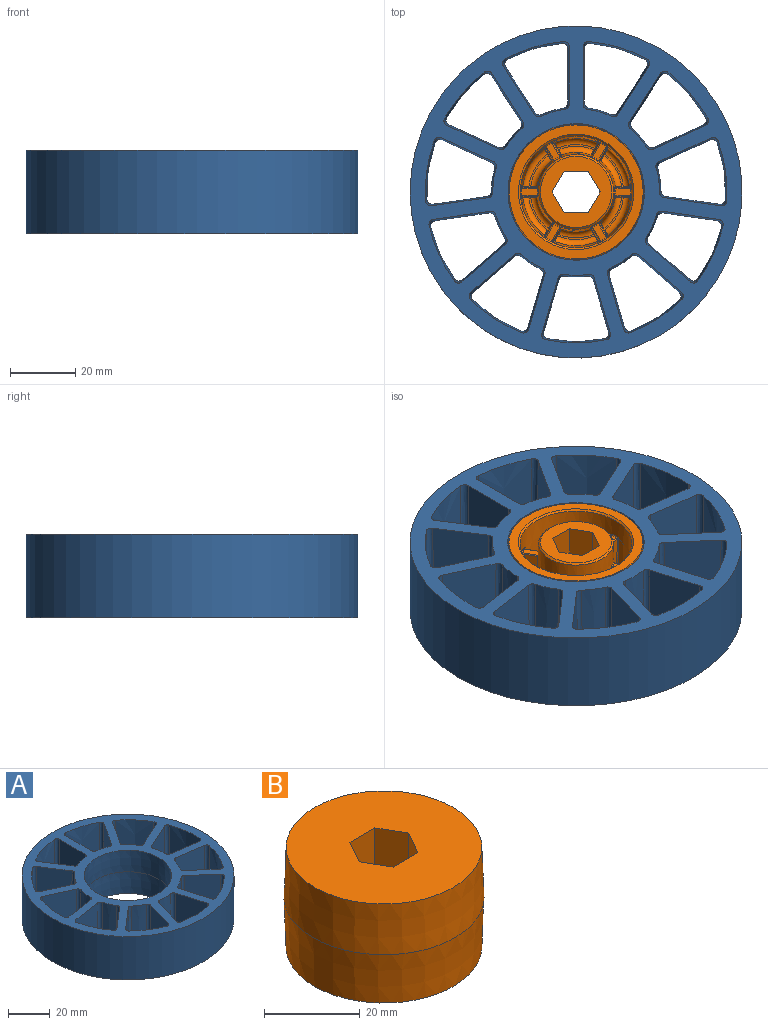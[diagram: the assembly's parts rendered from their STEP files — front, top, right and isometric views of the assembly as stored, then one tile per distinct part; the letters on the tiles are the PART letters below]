
ASSEMBLY  parts=2 mates=1
PART A: 93 faces, bbox 101.7x101.7x25.8 mm
  f0: cylinder r=50.8mm len=101.6mm, axis (0,0,-1), area 8107.3mm2, adj f25,f27
  f1: cone r=20.96mm half-angle=0.3deg, axis (0,0,1), area 1669.7mm2, adj f2,f27
  f2: cone r=20.89mm half-angle=0.3deg, axis (0,0,-1), area 1669.7mm2, adj f1,f25
  f3: cone r=45.72mm half-angle=1deg, axis (0,0,1), area 460.8mm2, adj f25,f27,f58,f59
  f4: cone r=25.97mm half-angle=1deg, axis (0,0,-1), area 186.1mm2, adj f25,f27,f80,f81
  f5: cone r=25.97mm half-angle=1deg, axis (0,0,-1), area 186.2mm2, adj f25,f27,f88,f89
  f6: cone r=45.72mm half-angle=1deg, axis (0,0,1), area 460.8mm2, adj f25,f27,f90,f91
  f7: cone r=45.72mm half-angle=1deg, axis (0,0,1), area 460.8mm2, adj f25,f27,f82,f83
  f8: cone r=25.97mm half-angle=1deg, axis (0,0,-1), area 186.2mm2, adj f25,f27,f76,f77
  f9: cone r=45.72mm half-angle=1deg, axis (0,0,1), area 460.8mm2, adj f25,f27,f78,f79
  f10: cone r=25.97mm half-angle=1deg, axis (0,0,-1), area 186.2mm2, adj f25,f27,f72,f73
  f11: cone r=45.72mm half-angle=1deg, axis (0,0,1), area 460.8mm2, adj f25,f27,f74,f75
  f12: cone r=25.97mm half-angle=1deg, axis (0,0,-1), area 186.2mm2, adj f25,f27,f68,f69
  f13: cone r=45.72mm half-angle=1deg, axis (0,0,1), area 460.8mm2, adj f25,f27,f70,f71
  f14: cone r=25.97mm half-angle=1deg, axis (0,0,-1), area 186.2mm2, adj f25,f27,f64,f65
  f15: cone r=45.72mm half-angle=1deg, axis (0,0,1), area 460.8mm2, adj f25,f27,f66,f67
  f16: cone r=25.97mm half-angle=1deg, axis (0,0,-1), area 186.2mm2, adj f25,f27,f60,f61
  f17: cone r=45.72mm half-angle=1deg, axis (0,0,1), area 460.8mm2, adj f25,f27,f62,f63
  f18: cone r=25.97mm half-angle=1deg, axis (0,0,-1), area 186.2mm2, adj f25,f27,f56,f57
  f19: cone r=25.97mm half-angle=1deg, axis (0,0,-1), area 186.2mm2, adj f25,f27,f52,f53
  f20: cone r=45.72mm half-angle=1deg, axis (0,0,1), area 460.8mm2, adj f25,f27,f54,f55
  f21: cone r=25.97mm half-angle=1deg, axis (0,0,-1), area 186.2mm2, adj f25,f27,f49,f50
  f22: cone r=45.72mm half-angle=1deg, axis (0,0,1), area 460.8mm2, adj f25,f27,f51,f92
  f23: plane 25.4x17.56mm, normal (1,0,0.02), area 435mm2, adj f25,f27,f85,f86
  f24: plane 25.4x17.56mm, normal (-1,0,0.02), area 435mm2, adj f25,f27,f50,f92
  f25: plane 101.66x101.66mm, normal (0,0,1), area 3063.9mm2, adj f0,f2,f3,f4,f5,f6,f7,f8
  f26: cone r=25.97mm half-angle=1deg, axis (0,0,-1), area 186.2mm2, adj f25,f27,f86,f87
  f27: plane 101.66x101.66mm, normal (0,0,-1), area 3415.8mm2, adj f0,f1,f3,f4,f5,f6,f7,f8
  f28: cone r=45.72mm half-angle=1deg, axis (0,0,1), area 460.8mm2, adj f25,f27,f84,f85
  f29: plane 25.4x14.77mm, normal (0.84,0.54,0.02), area 435mm2, adj f25,f27,f49,f51
  f30: plane 25.4x14.77mm, normal (-0.84,-0.54,0.02), area 435mm2, adj f25,f27,f53,f54
  f31: plane 25.4x15.97mm, normal (0.42,0.91,0.02), area 435mm2, adj f25,f27,f52,f55
  f32: plane 25.4x15.97mm, normal (-0.42,-0.91,0.02), area 435mm2, adj f25,f27,f57,f58
  f33: plane 25.4x17.38mm, normal (-0.14,0.99,0.02), area 435mm2, adj f25,f27,f56,f59
  f34: plane 25.4x17.38mm, normal (0.14,-0.99,0.02), area 435mm2, adj f25,f27,f61,f62
  f35: plane 25.4x13.27mm, normal (-0.65,0.76,0.02), area 435mm2, adj f25,f27,f60,f63
  f36: plane 25.4x13.27mm, normal (0.65,-0.76,0.02), area 435mm2, adj f25,f27,f65,f66
  f37: plane 25.4x16.85mm, normal (-0.96,0.28,0.02), area 435mm2, adj f25,f27,f64,f67
  f38: plane 25.4x16.85mm, normal (0.96,-0.28,0.02), area 435mm2, adj f25,f27,f69,f70
  f39: plane 25.4x16.85mm, normal (-0.96,-0.28,0.02), area 435mm2, adj f25,f27,f68,f71
  f40: plane 25.4x16.85mm, normal (0.96,0.28,0.02), area 435mm2, adj f25,f27,f73,f74
  f41: plane 25.4x13.27mm, normal (-0.65,-0.76,0.02), area 435mm2, adj f25,f27,f72,f75
  f42: plane 25.4x13.27mm, normal (0.65,0.76,0.02), area 435mm2, adj f25,f27,f77,f78
  f43: plane 25.4x17.38mm, normal (-0.14,-0.99,0.02), area 435mm2, adj f25,f27,f76,f79
  f44: plane 25.4x17.38mm, normal (0.14,0.99,0.02), area 435mm2, adj f25,f27,f81,f82
  f45: plane 25.4x15.97mm, normal (0.42,-0.91,0.02), area 435mm2, adj f25,f27,f80,f83
  f46: plane 25.4x15.97mm, normal (-0.42,0.91,0.02), area 435mm2, adj f25,f27,f89,f90
  f47: plane 25.4x14.77mm, normal (0.84,-0.54,0.02), area 435mm2, adj f25,f27,f88,f91
  f48: plane 25.4x14.77mm, normal (-0.84,0.54,0.02), area 435mm2, adj f25,f27,f84,f87
  f49: bspline ~25.41x2.15mm, area 57.6mm2, adj f21,f25,f27,f29
  f50: bspline ~25.41x1.96mm, area 57.6mm2, adj f21,f24,f25,f27
  f51: bspline ~25.41x2.43mm, area 66.9mm2, adj f22,f25,f27,f29
  f52: bspline ~25.41x2.17mm, area 57.6mm2, adj f19,f25,f27,f31
  f53: bspline ~25.41x2.15mm, area 57.6mm2, adj f19,f25,f27,f30
  f54: bspline ~25.75x2.43mm, area 66.9mm2, adj f20,f25,f27,f30
  f55: bspline ~25.75x2.44mm, area 66.9mm2, adj f20,f25,f27,f31
  f56: bspline ~25.73x1.95mm, area 57.6mm2, adj f18,f25,f27,f33
  f57: bspline ~25.73x2.13mm, area 57.6mm2, adj f18,f25,f27,f32
  f58: bspline ~25.75x2.41mm, area 66.9mm2, adj f3,f25,f27,f32
  f59: bspline ~25.41x2.23mm, area 66.9mm2, adj f3,f25,f27,f33
  f60: bspline ~25.73x2.13mm, area 57.6mm2, adj f16,f25,f27,f35
  f61: bspline ~25.41x2.07mm, area 57.6mm2, adj f16,f25,f27,f34
  f62: bspline ~25.41x2.31mm, area 66.9mm2, adj f17,f25,f27,f34
  f63: bspline ~25.75x2.4mm, area 66.9mm2, adj f17,f25,f27,f35
  f64: bspline ~25.73x2.14mm, area 57.6mm2, adj f14,f25,f27,f37
  f65: bspline ~25.73x2.09mm, area 57.6mm2, adj f14,f25,f27,f36
  f66: bspline ~25.41x2.36mm, area 66.9mm2, adj f15,f25,f27,f36
  f67: bspline ~25.75x2.4mm, area 66.9mm2, adj f15,f25,f27,f37
  f68: bspline ~25.41x2.05mm, area 57.6mm2, adj f12,f25,f27,f39
  f69: bspline ~25.41x2.05mm, area 57.6mm2, adj f12,f25,f27,f38
  f70: bspline ~25.41x2.34mm, area 66.9mm2, adj f13,f25,f27,f38
  f71: bspline ~25.41x2.34mm, area 66.9mm2, adj f13,f25,f27,f39
  f72: bspline ~25.73x2.09mm, area 57.6mm2, adj f10,f25,f27,f41
  f73: bspline ~25.73x2.14mm, area 57.6mm2, adj f10,f25,f27,f40
  f74: bspline ~25.75x2.4mm, area 66.9mm2, adj f11,f25,f27,f40
  f75: bspline ~25.41x2.36mm, area 66.9mm2, adj f11,f25,f27,f41
  f76: bspline ~25.41x2.07mm, area 57.6mm2, adj f8,f25,f27,f43
  f77: bspline ~25.73x2.13mm, area 57.6mm2, adj f8,f25,f27,f42
  f78: bspline ~25.75x2.4mm, area 66.9mm2, adj f9,f25,f27,f42
  f79: bspline ~25.41x2.31mm, area 66.9mm2, adj f9,f25,f27,f43
  f80: bspline ~25.73x2.13mm, area 57.6mm2, adj f4,f25,f27,f45
  f81: bspline ~25.41x1.94mm, area 57.6mm2, adj f4,f25,f27,f44
  f82: bspline ~25.41x2.23mm, area 66.9mm2, adj f7,f25,f27,f44
  f83: bspline ~25.75x2.41mm, area 66.9mm2, adj f7,f25,f27,f45
  f84: bspline ~25.41x2.43mm, area 66.9mm2, adj f25,f27,f28,f48
  f85: bspline ~25.41x2.18mm, area 66.9mm2, adj f23,f25,f27,f28
  f86: bspline ~25.41x1.96mm, area 57.6mm2, adj f23,f25,f26,f27
  f87: bspline ~25.41x2.15mm, area 57.6mm2, adj f25,f26,f27,f48
  f88: bspline ~25.41x2.15mm, area 57.6mm2, adj f5,f25,f27,f47
  f89: bspline ~25.41x2.17mm, area 57.6mm2, adj f5,f25,f27,f46
  f90: bspline ~25.75x2.44mm, area 66.9mm2, adj f6,f25,f27,f46
  f91: bspline ~25.75x2.43mm, area 66.9mm2, adj f6,f25,f27,f47
  f92: bspline ~25.41x2.18mm, area 66.9mm2, adj f22,f24,f25,f27
PART B: 159 faces, bbox 41.9x41.9x25.4 mm
  f0: torus R=16.68mm, axis (0,0,1), area 0.8mm2, adj f6,f31,f40,f45
  f1: torus R=11.9mm, axis (0,0,1), area 0.8mm2, adj f7,f31,f36,f41
  f2: cone r=20.24mm half-angle=2deg, axis (0,0,-1), area 1655.4mm2, adj f3,f25
  f3: cone r=20.96mm half-angle=2deg, axis (0,0,1), area 1655.4mm2, adj f2,f26
  f4: cone r=10.9mm half-angle=47deg, axis (0,0,1), area 52.3mm2, adj f7,f24
  f5: cone r=17.13mm half-angle=45deg, axis (0,0,-1), area 81.3mm2, adj f6,f26
  f6: cone r=16.46mm half-angle=2deg, axis (0,0,-1), area 1757.7mm2, adj f0,f5,f9,f12,f15,f18,f21,f27
  f7: cone r=11.43mm half-angle=2deg, axis (0,0,1), area 1163.6mm2, adj f1,f4,f8,f11,f14,f17,f20,f23
  f8: torus R=14.02mm, axis (0,0,-1), area 29mm2, adj f7,f10,f32,f146
  f9: torus R=14.55mm, axis (0,0,-1), area 37.6mm2, adj f6,f10,f35,f151
  f10: plane 9.83x5.94mm, normal (0,0,-1), area 6mm2, adj f8,f9,f33,f149
  f11: torus R=14.02mm, axis (0,0,-1), area 29mm2, adj f7,f13,f128,f135
  f12: torus R=14.55mm, axis (0,0,-1), area 37.6mm2, adj f6,f13,f133,f138
  f13: plane 11.35x1.61mm, normal (0,0,-1), area 6mm2, adj f11,f12,f131,f136
  f14: torus R=14.02mm, axis (0,0,-1), area 29mm2, adj f7,f16,f110,f117
  f15: torus R=14.55mm, axis (0,0,-1), area 37.6mm2, adj f6,f16,f115,f120
  f16: plane 9.83x5.94mm, normal (0,0,-1), area 6mm2, adj f14,f15,f113,f118
  f17: torus R=14.02mm, axis (0,0,-1), area 29mm2, adj f7,f19,f92,f99
  f18: torus R=14.55mm, axis (0,0,-1), area 37.6mm2, adj f6,f19,f97,f102
  f19: plane 9.83x5.94mm, normal (0,0,-1), area 6mm2, adj f17,f18,f95,f100
  f20: torus R=14.02mm, axis (0,0,-1), area 29mm2, adj f7,f22,f74,f81
  f21: torus R=14.55mm, axis (0,0,-1), area 37.6mm2, adj f6,f22,f79,f84
  f22: plane 11.35x1.61mm, normal (0,0,-1), area 6mm2, adj f20,f21,f77,f82
  f23: torus R=14.02mm, axis (0,0,-1), area 29mm2, adj f7,f28,f42,f63
  f24: plane 21.81x21.81mm, normal (0,0,-1), area 232.7mm2, adj f4,f153,f154,f155,f156,f157,f158
  f25: plane 41.02x41.02mm, normal (0,0,1), area 1180.9mm2, adj f2,f153,f154,f155,f156,f157,f158
  f26: plane 41.02x41.02mm, normal (0,0,-1), area 342.7mm2, adj f3,f5
  f27: torus R=14.55mm, axis (0,0,-1), area 37.6mm2, adj f6,f28,f46,f66
  f28: plane 9.83x5.94mm, normal (0,0,-1), area 6mm2, adj f23,f27,f44,f64
  f29: plane 14.75x4.78mm, normal (0,-1,-0.02), area 61.7mm2, adj f39,f42,f43,f44,f46,f47
  f30: plane 14.74x4.78mm, normal (0,1,-0.02), area 61.7mm2, adj f32,f33,f34,f35,f37,f38
  f31: plane 4.82x2.04mm, normal (0,0,-1), area 9.8mm2, adj f0,f1,f38,f43
  f32: bspline ~1.91x1.84mm, area 1mm2, adj f8,f30,f33,f34
  f33: cylinder r=0.25mm len=0.53mm, axis (-1,0,0), area 0.2mm2, adj f10,f30,f32,f35
  f34: bspline ~13.15x0.68mm, area 4.8mm2, adj f7,f30,f32,f36
  f35: bspline ~1.95x1.85mm, area 1.2mm2, adj f9,f30,f33,f37
  f36: bspline ~0.5x0.5mm, area 0.2mm2, adj f1,f7,f34,f38
  f37: bspline ~13.15x0.74mm, area 5.6mm2, adj f6,f30,f35,f40
  f38: cylinder r=0.25mm len=4.83mm, axis (-1,0,0), area 1.9mm2, adj f30,f31,f36,f40
  f39: cylinder r=0.25mm len=13.15mm, axis (0.03,-0.02,1), area 4.8mm2, adj f7,f29,f41,f42
  f40: bspline ~0.53x0.51mm, area 0.2mm2, adj f0,f6,f37,f38
  f41: bspline ~0.5x0.5mm, area 0.2mm2, adj f1,f7,f39,f43
  f42: bspline ~1.91x1.84mm, area 1mm2, adj f23,f29,f39,f44
  f43: cylinder r=0.25mm len=4.83mm, axis (1,0,0), area 1.9mm2, adj f29,f31,f41,f45
  f44: cylinder r=0.25mm len=0.53mm, axis (1,0,0), area 0.2mm2, adj f28,f29,f42,f46
  f45: bspline ~0.53x0.51mm, area 0.2mm2, adj f0,f6,f43,f47
  f46: bspline ~1.95x1.85mm, area 1.2mm2, adj f27,f29,f44,f47
  f47: bspline ~13.15x0.74mm, area 5.6mm2, adj f6,f29,f45,f46
  f48: plane 14.75x4.14mm, normal (-0.87,-0.5,-0.02), area 61.7mm2, adj f71,f74,f76,f77,f79,f80
  f49: plane 14.74x4.14mm, normal (0.87,0.5,-0.02), area 61.7mm2, adj f63,f64,f65,f66,f68,f69
  f50: plane 5.17x4.16mm, normal (0,0,-1), area 9.8mm2, adj f69,f70,f75,f76
  f51: plane 14.75x4.14mm, normal (-0.87,0.5,-0.02), area 61.7mm2, adj f89,f92,f94,f95,f97,f98
  f52: plane 14.74x4.14mm, normal (0.87,-0.5,-0.02), area 61.7mm2, adj f81,f82,f83,f84,f86,f87
  f53: plane 5.17x4.16mm, normal (0,0,-1), area 9.8mm2, adj f87,f88,f93,f94
  f54: plane 14.75x4.78mm, normal (0,1,-0.02), area 61.7mm2, adj f107,f110,f112,f113,f115,f116
  f55: plane 14.74x4.78mm, normal (0,-1,-0.02), area 61.7mm2, adj f99,f100,f101,f102,f104,f105
  f56: plane 4.82x2.04mm, normal (0,0,-1), area 9.8mm2, adj f105,f106,f111,f112
  f57: plane 14.75x4.14mm, normal (0.87,0.5,-0.02), area 61.7mm2, adj f125,f128,f130,f131,f133,f134
  f58: plane 14.74x4.14mm, normal (-0.87,-0.5,-0.02), area 61.7mm2, adj f117,f118,f119,f120,f122,f123
  f59: plane 5.17x4.16mm, normal (0,0,-1), area 9.8mm2, adj f123,f124,f129,f130
  f60: plane 14.75x4.14mm, normal (0.87,-0.5,-0.02), area 61.7mm2, adj f143,f146,f148,f149,f151,f152
  f61: plane 14.74x4.14mm, normal (-0.87,0.5,-0.02), area 61.7mm2, adj f135,f136,f137,f138,f140,f141
  f62: plane 5.17x4.16mm, normal (0,0,-1), area 9.8mm2, adj f141,f142,f147,f148
  f63: bspline ~1.84x1.75mm, area 1mm2, adj f23,f49,f64,f65
  f64: cylinder r=0.25mm len=0.59mm, axis (-0.5,0.87,0), area 0.2mm2, adj f28,f49,f63,f66
  f65: bspline ~13.15x0.59mm, area 4.8mm2, adj f7,f49,f63,f67
  f66: bspline ~1.85x1.83mm, area 1.2mm2, adj f27,f49,f64,f68
  f67: bspline ~0.5x0.49mm, area 0.2mm2, adj f7,f65,f69,f70
  f68: bspline ~13.15x0.66mm, area 5.6mm2, adj f6,f49,f66,f72
  f69: cylinder r=0.25mm len=4.31mm, axis (-0.5,0.87,0), area 1.9mm2, adj f49,f50,f67,f72
  f70: torus R=11.9mm, axis (0,0,1), area 0.8mm2, adj f7,f50,f67,f73
  f71: cylinder r=0.25mm len=13.15mm, axis (0,-0.04,1), area 4.8mm2, adj f7,f48,f73,f74
  f72: bspline ~0.56x0.51mm, area 0.2mm2, adj f6,f68,f69,f75
  f73: bspline ~0.56x0.5mm, area 0.2mm2, adj f7,f70,f71,f76
  f74: bspline ~1.84x1.77mm, area 1mm2, adj f20,f48,f71,f77
  f75: torus R=16.68mm, axis (0,0,1), area 0.8mm2, adj f6,f50,f72,f78
  f76: cylinder r=0.25mm len=4.31mm, axis (0.5,-0.87,0), area 1.9mm2, adj f48,f50,f73,f78
  f77: cylinder r=0.25mm len=0.59mm, axis (0.5,-0.87,0), area 0.2mm2, adj f22,f48,f74,f79
  f78: bspline ~0.51x0.48mm, area 0.2mm2, adj f6,f75,f76,f80
  f79: bspline ~1.85x1.79mm, area 1.2mm2, adj f21,f48,f77,f80
  f80: bspline ~13.16x0.7mm, area 5.6mm2, adj f6,f48,f78,f79
  f81: bspline ~1.84x1.77mm, area 1mm2, adj f20,f52,f82,f83
  f82: cylinder r=0.25mm len=0.59mm, axis (-0.5,-0.87,0), area 0.2mm2, adj f22,f52,f81,f84
  f83: bspline ~13.15x0.61mm, area 4.8mm2, adj f7,f52,f81,f85
  f84: bspline ~1.85x1.79mm, area 1.2mm2, adj f21,f52,f82,f86
  f85: bspline ~0.56x0.5mm, area 0.2mm2, adj f7,f83,f87,f88
  f86: bspline ~13.15x0.66mm, area 5.6mm2, adj f6,f52,f84,f90
  f87: cylinder r=0.25mm len=4.31mm, axis (0.5,0.87,0), area 1.9mm2, adj f52,f53,f85,f90
  f88: torus R=11.9mm, axis (0,0,1), area 0.8mm2, adj f7,f53,f85,f91
  f89: cylinder r=0.25mm len=13.15mm, axis (-0.03,-0.02,1), area 4.8mm2, adj f7,f51,f91,f92
  f90: bspline ~0.51x0.48mm, area 0.2mm2, adj f6,f86,f87,f93
  f91: bspline ~0.5x0.49mm, area 0.2mm2, adj f7,f88,f89,f94
  f92: bspline ~1.84x1.75mm, area 1mm2, adj f17,f51,f89,f95
  f93: torus R=16.68mm, axis (0,0,1), area 0.8mm2, adj f6,f53,f90,f96
  f94: cylinder r=0.25mm len=4.31mm, axis (-0.5,-0.87,0), area 1.9mm2, adj f51,f53,f91,f96
  f95: cylinder r=0.25mm len=0.59mm, axis (0.5,0.87,0), area 0.2mm2, adj f19,f51,f92,f97
  f96: bspline ~0.56x0.51mm, area 0.2mm2, adj f6,f93,f94,f98
  f97: bspline ~1.85x1.83mm, area 1.2mm2, adj f18,f51,f95,f98
  f98: bspline ~13.15x0.66mm, area 5.6mm2, adj f6,f51,f96,f97
  f99: bspline ~1.91x1.84mm, area 1mm2, adj f17,f55,f100,f101
  f100: cylinder r=0.25mm len=0.53mm, axis (-1,0,0), area 0.2mm2, adj f19,f55,f99,f102
  f101: bspline ~13.15x0.68mm, area 4.8mm2, adj f7,f55,f99,f103
  f102: bspline ~1.95x1.85mm, area 1.2mm2, adj f18,f55,f100,f104
  f103: bspline ~0.5x0.5mm, area 0.2mm2, adj f7,f101,f105,f106
  f104: bspline ~13.15x0.74mm, area 5.6mm2, adj f6,f55,f102,f108
  f105: cylinder r=0.25mm len=4.83mm, axis (1,0,0), area 1.9mm2, adj f55,f56,f103,f108
  f106: torus R=11.9mm, axis (0,0,1), area 0.8mm2, adj f7,f56,f103,f109
  f107: cylinder r=0.25mm len=13.15mm, axis (-0.03,0.02,1), area 4.8mm2, adj f7,f54,f109,f110
  f108: bspline ~0.53x0.51mm, area 0.2mm2, adj f6,f104,f105,f111
  f109: bspline ~0.5x0.5mm, area 0.2mm2, adj f7,f106,f107,f112
  f110: bspline ~1.91x1.84mm, area 1mm2, adj f14,f54,f107,f113
  f111: torus R=16.68mm, axis (0,0,1), area 0.8mm2, adj f6,f56,f108,f114
  f112: cylinder r=0.25mm len=4.83mm, axis (-1,0,0), area 1.9mm2, adj f54,f56,f109,f114
  f113: cylinder r=0.25mm len=0.53mm, axis (1,0,0), area 0.2mm2, adj f16,f54,f110,f115
  f114: bspline ~0.53x0.51mm, area 0.2mm2, adj f6,f111,f112,f116
  f115: bspline ~1.95x1.85mm, area 1.2mm2, adj f15,f54,f113,f116
  f116: bspline ~13.15x0.74mm, area 5.6mm2, adj f6,f54,f114,f115
  f117: bspline ~1.84x1.75mm, area 1mm2, adj f14,f58,f118,f119
  f118: cylinder r=0.25mm len=0.59mm, axis (-0.5,0.87,0), area 0.2mm2, adj f16,f58,f117,f120
  f119: bspline ~13.15x0.59mm, area 4.8mm2, adj f7,f58,f117,f121
  f120: bspline ~1.85x1.83mm, area 1.2mm2, adj f15,f58,f118,f122
  f121: bspline ~0.5x0.49mm, area 0.2mm2, adj f7,f119,f123,f124
  f122: bspline ~13.15x0.66mm, area 5.6mm2, adj f6,f58,f120,f126
  f123: cylinder r=0.25mm len=4.31mm, axis (0.5,-0.87,0), area 1.9mm2, adj f58,f59,f121,f126
  f124: torus R=11.9mm, axis (0,0,1), area 0.8mm2, adj f7,f59,f121,f127
  f125: cylinder r=0.25mm len=13.15mm, axis (0,0.04,1), area 4.8mm2, adj f7,f57,f127,f128
  f126: bspline ~0.56x0.51mm, area 0.2mm2, adj f6,f122,f123,f129
  f127: bspline ~0.56x0.5mm, area 0.2mm2, adj f7,f124,f125,f130
  f128: bspline ~1.84x1.77mm, area 1mm2, adj f11,f57,f125,f131
  f129: torus R=16.68mm, axis (0,0,1), area 0.8mm2, adj f6,f59,f126,f132
  f130: cylinder r=0.25mm len=4.31mm, axis (-0.5,0.87,0), area 1.9mm2, adj f57,f59,f127,f132
  f131: cylinder r=0.25mm len=0.59mm, axis (0.5,-0.87,0), area 0.2mm2, adj f13,f57,f128,f133
  f132: bspline ~0.51x0.48mm, area 0.2mm2, adj f6,f129,f130,f134
  f133: bspline ~1.85x1.79mm, area 1.2mm2, adj f12,f57,f131,f134
  f134: bspline ~13.16x0.7mm, area 5.6mm2, adj f6,f57,f132,f133
  f135: bspline ~1.84x1.77mm, area 1mm2, adj f11,f61,f136,f137
  f136: cylinder r=0.25mm len=0.59mm, axis (0.5,0.87,0), area 0.2mm2, adj f13,f61,f135,f138
  f137: bspline ~13.15x0.68mm, area 4.8mm2, adj f7,f61,f135,f139
  f138: bspline ~1.85x1.79mm, area 1.2mm2, adj f12,f61,f136,f140
  f139: bspline ~0.56x0.5mm, area 0.2mm2, adj f7,f137,f141,f142
  f140: bspline ~13.15x0.66mm, area 5.6mm2, adj f6,f61,f138,f144
  f141: cylinder r=0.25mm len=4.31mm, axis (-0.5,-0.87,0), area 1.9mm2, adj f61,f62,f139,f144
  f142: torus R=11.9mm, axis (0,0,1), area 0.8mm2, adj f7,f62,f139,f145
  f143: cylinder r=0.25mm len=13.15mm, axis (0.03,0.02,1), area 4.8mm2, adj f7,f60,f145,f146
  f144: bspline ~0.51x0.48mm, area 0.2mm2, adj f6,f140,f141,f147
  f145: bspline ~0.5x0.49mm, area 0.2mm2, adj f7,f142,f143,f148
  f146: bspline ~1.84x1.75mm, area 1mm2, adj f8,f60,f143,f149
  f147: torus R=16.68mm, axis (0,0,1), area 0.8mm2, adj f6,f62,f144,f150
  f148: cylinder r=0.25mm len=4.31mm, axis (0.5,0.87,0), area 1.9mm2, adj f60,f62,f145,f150
  f149: cylinder r=0.25mm len=0.59mm, axis (-0.5,-0.87,0), area 0.2mm2, adj f10,f60,f146,f151
  f150: bspline ~0.56x0.51mm, area 0.2mm2, adj f6,f147,f148,f152
  f151: bspline ~1.85x1.83mm, area 1.2mm2, adj f9,f60,f149,f152
  f152: bspline ~13.15x0.66mm, area 5.6mm2, adj f6,f60,f150,f151
  f153: plane 25.4x6.38mm, normal (0.87,0.5,0), area 187mm2, adj f24,f25,f154,f158
  f154: plane 25.4x7.36mm, normal (0,1,0), area 187mm2, adj f24,f25,f153,f155
  f155: plane 25.4x6.38mm, normal (-0.87,0.5,0), area 187mm2, adj f24,f25,f154,f156
  f156: plane 25.4x6.38mm, normal (-0.87,-0.5,0), area 187mm2, adj f24,f25,f155,f157
  f157: plane 25.4x7.36mm, normal (0,-1,0), area 187mm2, adj f24,f25,f156,f158
  f158: plane 25.4x6.38mm, normal (0.87,-0.5,0), area 187mm2, adj f24,f25,f153,f157
PLACE A t=(-16.24,3.85,18.65)mm
PLACE B rot(axis=(0,-1,0),180deg) t=(-16.24,3.85,5.95)mm
MATE fastened B.f3 <-> A.f0  axis (0,0,1) through (-16.24,3.85,5.95)mm
